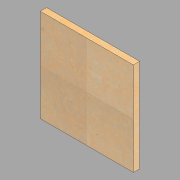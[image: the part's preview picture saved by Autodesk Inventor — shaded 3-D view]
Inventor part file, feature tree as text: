
AUTODESK INVENTOR PART (.ipt)
format: ipt  version: 2022.1 (Build 261234020, 234B)  size: 101,888 bytes
history: native  units: in
note: dims shown in document units (in); Inventor stores cm internally (conversion verified against a paired STEP export)
features: extrude x1, sketch x1
ambient origin geometry x8: Origin, YZ Plane, XZ Plane, XY Plane, X Axis, Y Axis, Z Axis, Center Point
bodies: Solid1 (feature_tree)
feature tree (2):
  extrude  "Extrusion1"  Depth=29.625in
  sketch  "Sketch1"  dims[d0=29.625in d1=29.625in d2=2.0in d3=0.0in]
